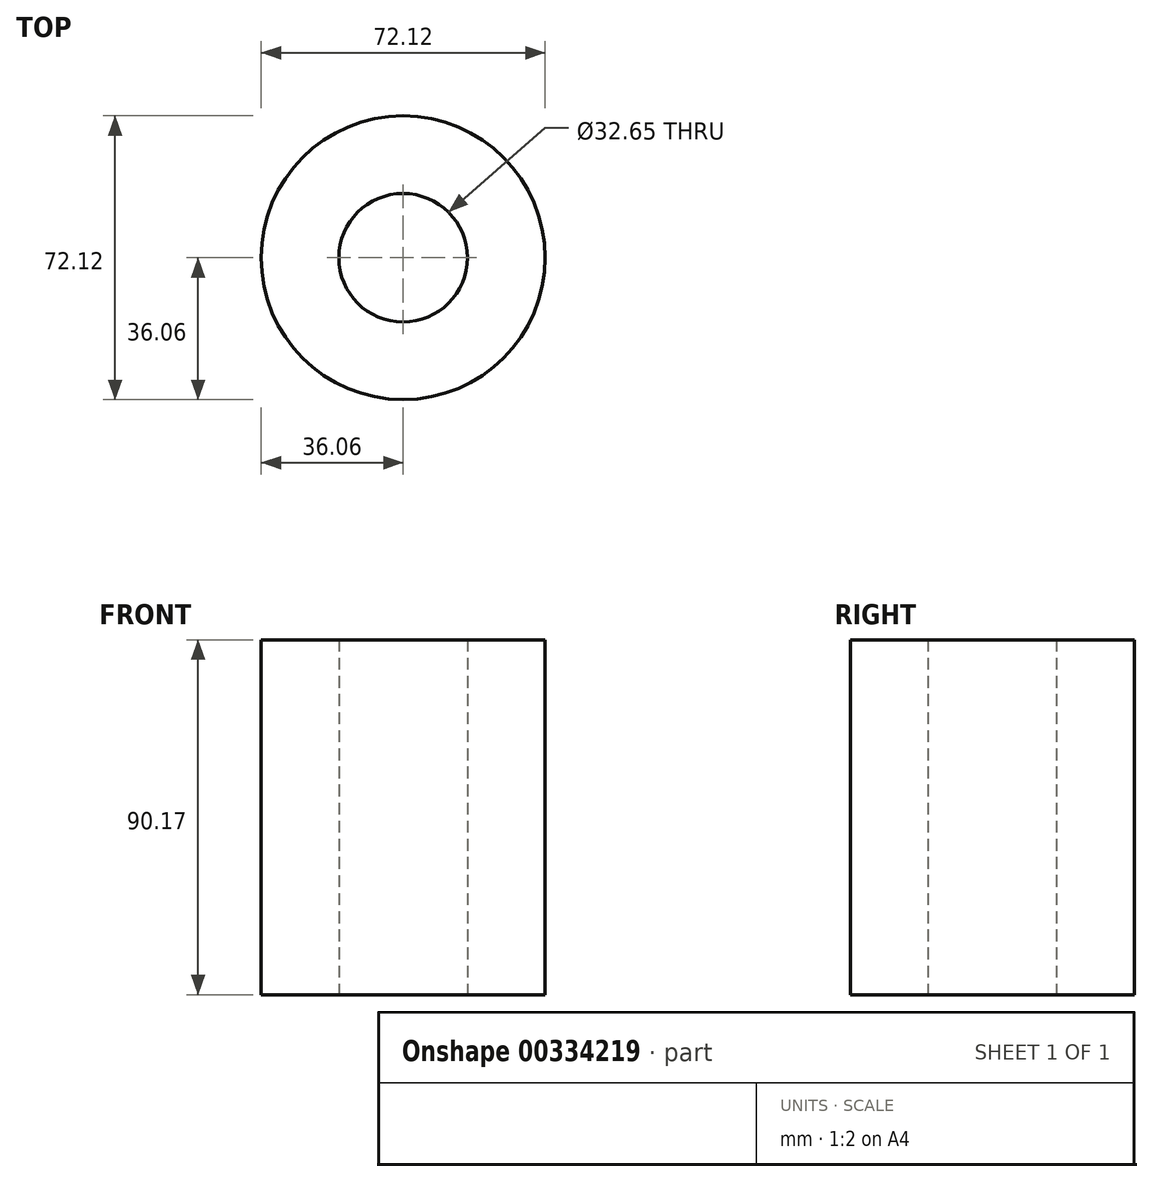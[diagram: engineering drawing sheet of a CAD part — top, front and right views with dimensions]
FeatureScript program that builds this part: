
annotation { "Feature Type Name" : "Feature", "Feature Type Description" : "" }
export const myFeature = defineFeature(function(context is Context, id is Id, definition is map)
    precondition{}
    {
        {
            var Q0;
            Q0=qCreatedBy(makeId("Top.planeOp"),FACE);
            var sketch = newSketch(context, id + "F0", { "sketchPlane" : qUnion([Q0])});
            skCircle(sketch, "E0", {"center": v(0, 0) * mm, "radius": 36.06 * mm});
            skSolve(sketch);
        }
        {
            var Q0;
            Q0 = qSketchRegion(id + "F0", true);
            extrude(context, id + "F1", {"entities" : qUnion([Q0]), "depth" : 90.17 * mm});
        }
        {
            var Q0;
            Q0=makeQuery(id+"F1.opExtrude","CAP_FACE",FACE,{"disambiguationData":[OSD([sQuery(id+"F0.wireOp",EDGE,"E0")])],"isStart":true});
            var sketch = newSketch(context, id + "F2", { "sketchPlane" : qUnion([Q0])});
            skCircle(sketch, "E1", {"center": v(0, 0) * mm, "radius": 16.32 * mm});
            skSolve(sketch);
        }
        {
            var Q0;
            Q0=makeQuery(id+"F2.imprint","IMPRINT",FACE,{"disambiguationData":[TD([[makeQuery(id+"F2.imprint","IMPRINT",EDGE,{"derivedFrom":sQuery(id+"F2.wireOp",EDGE,"E1")}),1.0]])]});
            extrude(context, id + "F3", {"entities" : qUnion([Q0]), "operationType" : NewBodyOperationType.REMOVE, "endBound" : BoundingType.UP_TO_NEXT, "oppositeDirection" : true, "depth" : 25.4 * mm});
        }
    });
